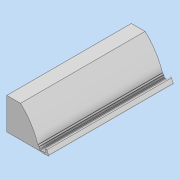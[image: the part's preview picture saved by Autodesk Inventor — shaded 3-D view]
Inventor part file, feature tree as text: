
AUTODESK INVENTOR PART (.ipt)
format: ipt  version: 2020 (Build 240168000, 168)  size: 153,088 bytes
history: native  units: mm
features: other x1, sweep x1, fillet x1, sketch x1
ambient origin geometry x8: Origin, YZ Plane, XZ Plane, XY Plane, X Axis, Y Axis, Z Axis, Center Point
bodies: Body1 (feature_tree)
feature tree (4):
  other  "實體1"
  sweep  "掃掠1"
  fillet  "圓角1"  Radius=1.7mm
  sketch  "草圖3"
